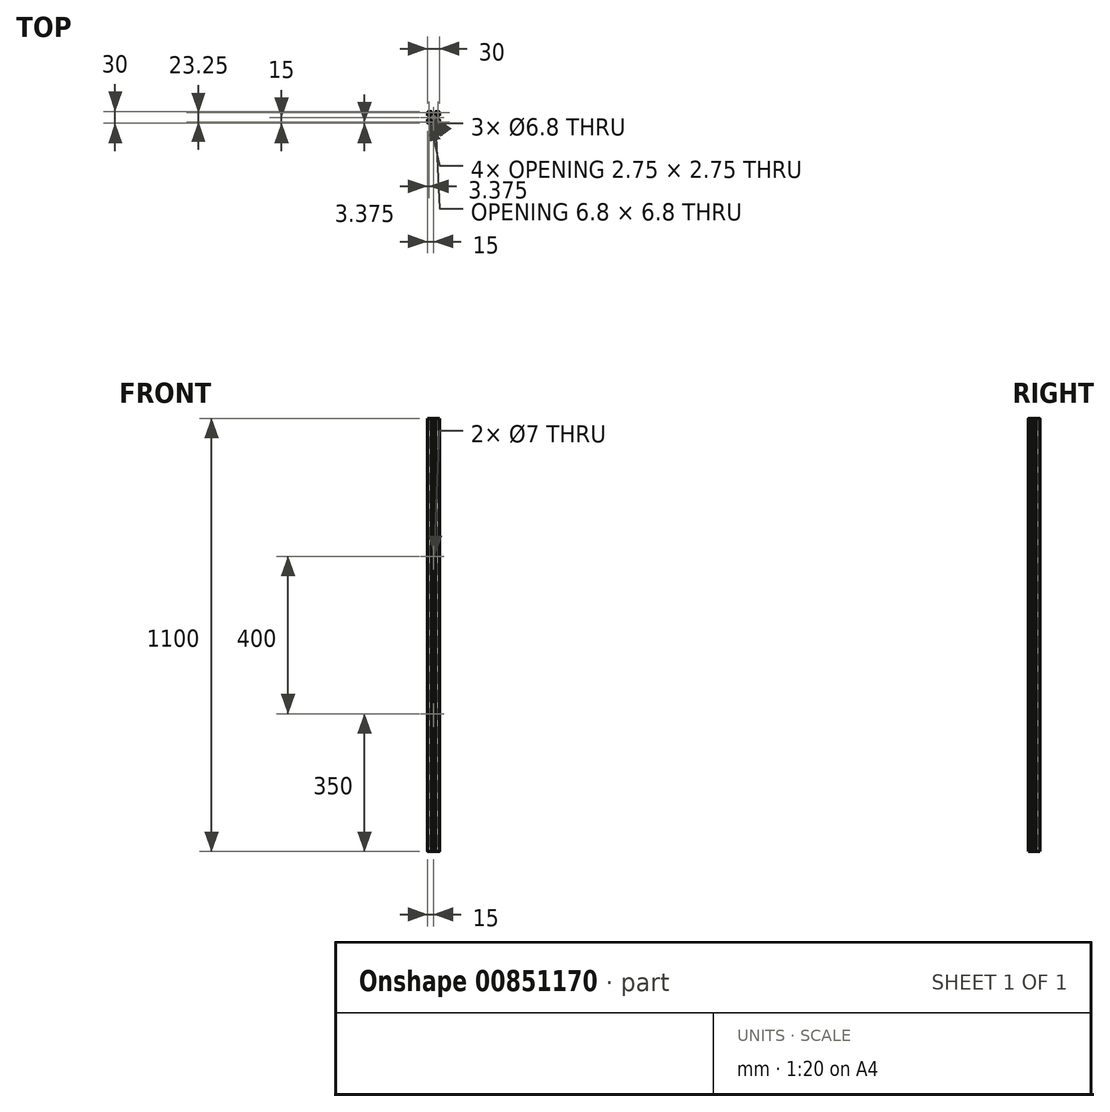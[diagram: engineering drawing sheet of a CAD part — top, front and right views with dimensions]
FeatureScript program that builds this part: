
annotation { "Feature Type Name" : "Feature", "Feature Type Description" : "" }
export const myFeature = defineFeature(function(context is Context, id is Id, definition is map)
    precondition{}
    {
        {
            var Q0;
            Q0=qCreatedBy(makeId("Top.planeOp"),FACE);
            var sketch = newSketch(context, id + "F0", { "sketchPlane" : qUnion([Q0])});
            skLineSegment(sketch, "E0", {"start": v(-5.1, 15) * mm, "end": v(-5.1, 14) * mm});
            skLineSegment(sketch, "E1", {"start": v(-5.1, 14) * mm, "end": v(-4.1, 14) * mm});
            skLineSegment(sketch, "E2", {"start": v(-4.1, 14) * mm, "end": v(-4.1, 13) * mm});
            skLineSegment(sketch, "E3", {"start": v(-4.1, 13) * mm, "end": v(-8.25, 13) * mm});
            skLineSegment(sketch, "E4", {"start": v(-5.1, 15) * mm, "end": v(-12.5, 15) * mm});
            skArc(sketch, "E5", {"start": v(-12.5, 15) * mm, "mid": v(-14.27, 14.27) * mm, "end": v(-15, 12.5) * mm});
            skLineSegment(sketch, "E6", {"start": v(-15, 12.5) * mm, "end": v(-15, 5.1) * mm});
            skLineSegment(sketch, "E7", {"start": v(-15, 5.1) * mm, "end": v(-14, 5.1) * mm});
            skLineSegment(sketch, "E8", {"start": v(-14, 5.1) * mm, "end": v(-14, 4.1) * mm});
            skLineSegment(sketch, "E9", {"start": v(-14, 4.1) * mm, "end": v(-13, 4.1) * mm});
            skLineSegment(sketch, "E10", {"start": v(-13, 4.1) * mm, "end": v(-13, 8.25) * mm});
            skArc(sketch, "E11", {"start": v(-3.4, 0) * mm, "mid": v(-2.4, 2.4) * mm, "end": v(0, 3.4) * mm});
            skLineSegment(sketch, "E12", {"start": v(-5.5, 0) * mm, "end": v(-3.4, 0) * mm});
            skLineSegment(sketch, "E13", {"start": v(0, 3.4) * mm, "end": v(0, 5.5) * mm});
            skLineSegment(sketch, "E14", {"start": v(-8.25, 13) * mm, "end": v(-8.25, 9.7) * mm});
            skLineSegment(sketch, "E15", {"start": v(-8.25, 9.7) * mm, "end": v(-4.35, 5.8) * mm});
            skLineSegment(sketch, "E16", {"start": v(-4.35, 5.8) * mm, "end": v(-0.5, 5.8) * mm});
            skLineSegment(sketch, "E17", {"start": v(-0.5, 5.8) * mm, "end": v(0, 5.5) * mm});
            skLineSegment(sketch, "E18", {"start": v(-5.5, 0) * mm, "end": v(-5.8, 0.5) * mm});
            skLineSegment(sketch, "E19", {"start": v(-5.8, 0.5) * mm, "end": v(-5.8, 4.35) * mm});
            skLineSegment(sketch, "E20", {"start": v(-5.8, 4.35) * mm, "end": v(-9.7, 8.25) * mm});
            skLineSegment(sketch, "E21", {"start": v(-9.7, 8.25) * mm, "end": v(-13, 8.25) * mm});
            skLineSegment(sketch, "E22", {"start": v(-12.5, 13) * mm, "end": v(-10.75, 13) * mm});
            skArc(sketch, "E23", {"start": v(-10.75, 13) * mm, "mid": v(-10.4, 12.85) * mm, "end": v(-10.25, 12.5) * mm});
            skLineSegment(sketch, "E24", {"start": v(-10.25, 12.5) * mm, "end": v(-10.25, 10.75) * mm});
            skArc(sketch, "E25", {"start": v(-10.25, 10.75) * mm, "mid": v(-10.4, 10.4) * mm, "end": v(-10.75, 10.25) * mm});
            skLineSegment(sketch, "E26", {"start": v(-10.75, 10.25) * mm, "end": v(-12.5, 10.25) * mm});
            skArc(sketch, "E27", {"start": v(-12.5, 10.25) * mm, "mid": v(-12.85, 10.4) * mm, "end": v(-13, 10.75) * mm});
            skLineSegment(sketch, "E28", {"start": v(-13, 10.75) * mm, "end": v(-13, 12.5) * mm});
            skArc(sketch, "E29", {"start": v(-13, 12.5) * mm, "mid": v(-12.85, 12.85) * mm, "end": v(-12.5, 13) * mm});
            skSolve(sketch);
        }
        {
            var Q0;
            Q0=qSketchRegion(id+"F0",true);
            extrude(context, id + "F1", {"entities" : qUnion([Q0]), "endBound" : BoundingType.SYMMETRIC, "depth" : 1100 * mm, "offsetDistance" : 25 * mm});
        }
        {
            var Q0;
            Q0=makeQuery(id+"F1.opExtrude","SWEPT_BODY",BODY,{"disambiguationData":[OSD([sQuery(id+"F0.wireOp",EDGE,"E0"),sQuery(id+"F0.wireOp",EDGE,"E1"),sQuery(id+"F0.wireOp",EDGE,"E2"),sQuery(id+"F0.wireOp",EDGE,"E3"),sQuery(id+"F0.wireOp",EDGE,"E4"),sQuery(id+"F0.wireOp",EDGE,"E5"),sQuery(id+"F0.wireOp",EDGE,"E6"),sQuery(id+"F0.wireOp",EDGE,"E7"),sQuery(id+"F0.wireOp",EDGE,"E8"),sQuery(id+"F0.wireOp",EDGE,"E9"),sQuery(id+"F0.wireOp",EDGE,"E10"),sQuery(id+"F0.wireOp",EDGE,"E11"),sQuery(id+"F0.wireOp",EDGE,"E12"),sQuery(id+"F0.wireOp",EDGE,"E13"),sQuery(id+"F0.wireOp",EDGE,"E14"),sQuery(id+"F0.wireOp",EDGE,"E15"),sQuery(id+"F0.wireOp",EDGE,"E16"),sQuery(id+"F0.wireOp",EDGE,"E17"),sQuery(id+"F0.wireOp",EDGE,"E18"),sQuery(id+"F0.wireOp",EDGE,"E19"),sQuery(id+"F0.wireOp",EDGE,"E20"),sQuery(id+"F0.wireOp",EDGE,"E21"),sQuery(id+"F0.wireOp",EDGE,"E22"),sQuery(id+"F0.wireOp",EDGE,"E23"),sQuery(id+"F0.wireOp",EDGE,"E24"),sQuery(id+"F0.wireOp",EDGE,"E25"),sQuery(id+"F0.wireOp",EDGE,"E26"),sQuery(id+"F0.wireOp",EDGE,"E27"),sQuery(id+"F0.wireOp",EDGE,"E28"),sQuery(id+"F0.wireOp",EDGE,"E29")])]});
            var Q1;
            Q1=makeQuery(id+"F1.opExtrude","SWEPT_FACE",FACE,{"disambiguationData":[OSD([sQuery(id+"F0.wireOp",EDGE,"E13")])]});
            mirror(context, id + "F2", {"operationType" : NewBodyOperationType.ADD, "entities" : qUnion([Q0]), "mirrorPlane" : qUnion([Q1])});
        }
        {
            var Q0;
            Q0=makeQuery(id+"F1.opExtrude","SWEPT_BODY",BODY,{"disambiguationData":[OSD([sQuery(id+"F0.wireOp",EDGE,"E0"),sQuery(id+"F0.wireOp",EDGE,"E1"),sQuery(id+"F0.wireOp",EDGE,"E2"),sQuery(id+"F0.wireOp",EDGE,"E3"),sQuery(id+"F0.wireOp",EDGE,"E4"),sQuery(id+"F0.wireOp",EDGE,"E5"),sQuery(id+"F0.wireOp",EDGE,"E6"),sQuery(id+"F0.wireOp",EDGE,"E7"),sQuery(id+"F0.wireOp",EDGE,"E8"),sQuery(id+"F0.wireOp",EDGE,"E9"),sQuery(id+"F0.wireOp",EDGE,"E10"),sQuery(id+"F0.wireOp",EDGE,"E11"),sQuery(id+"F0.wireOp",EDGE,"E12"),sQuery(id+"F0.wireOp",EDGE,"E13"),sQuery(id+"F0.wireOp",EDGE,"E14"),sQuery(id+"F0.wireOp",EDGE,"E15"),sQuery(id+"F0.wireOp",EDGE,"E16"),sQuery(id+"F0.wireOp",EDGE,"E17"),sQuery(id+"F0.wireOp",EDGE,"E18"),sQuery(id+"F0.wireOp",EDGE,"E19"),sQuery(id+"F0.wireOp",EDGE,"E20"),sQuery(id+"F0.wireOp",EDGE,"E21"),sQuery(id+"F0.wireOp",EDGE,"E22"),sQuery(id+"F0.wireOp",EDGE,"E23"),sQuery(id+"F0.wireOp",EDGE,"E24"),sQuery(id+"F0.wireOp",EDGE,"E25"),sQuery(id+"F0.wireOp",EDGE,"E26"),sQuery(id+"F0.wireOp",EDGE,"E27"),sQuery(id+"F0.wireOp",EDGE,"E28"),sQuery(id+"F0.wireOp",EDGE,"E29")])]});
            var Q1;
            Q1=makeQuery(id+"F1.opExtrude","SWEPT_FACE",FACE,{"disambiguationData":[OSD([sQuery(id+"F0.wireOp",EDGE,"E12")])]});
            mirror(context, id + "F3", {"operationType" : NewBodyOperationType.ADD, "entities" : qUnion([Q0]), "mirrorPlane" : qUnion([Q1])});
        }
        {
            var Q0;
            Q0=makeQuery(id+"F3.opPattern","COPY",FACE,{"derivedFrom":makeQuery(id+"F2.opPattern","COPY",FACE,{"derivedFrom":makeQuery(id+"F1.opExtrude","SWEPT_FACE",FACE,{"disambiguationData":[OSD([sQuery(id+"F0.wireOp",EDGE,"E4")])]}),"instanceName":"1"}),"instanceName":"1"});
            var sketch = newSketch(context, id + "F4", { "sketchPlane" : qUnion([Q0])});
            skCircle(sketch, "E30", {"center": v(0, -200) * mm, "radius": 3.5 * mm});
            skCircle(sketch, "E31", {"center": v(0, 200) * mm, "radius": 3.5 * mm});
            skSolve(sketch);
        }
        {
            var Q0;
            Q0=makeQuery(id+"F4.imprint","IMPRINT",FACE,{"disambiguationData":[TD([[makeQuery(id+"F4.imprint","IMPRINT",EDGE,{"derivedFrom":sQuery(id+"F4.wireOp",EDGE,"E31")}),1.0]])]});
            var Q1;
            Q1=makeQuery(id+"F4.imprint","IMPRINT",FACE,{"disambiguationData":[TD([[makeQuery(id+"F4.imprint","IMPRINT",EDGE,{"derivedFrom":sQuery(id+"F4.wireOp",EDGE,"E30")}),1.0]])]});
            extrude(context, id + "F5", {"entities" : qUnion([Q0, Q1]), "operationType" : NewBodyOperationType.REMOVE, "oppositeDirection" : true, "depth" : 50 * mm, "offsetDistance" : 25 * mm});
        }
    });
